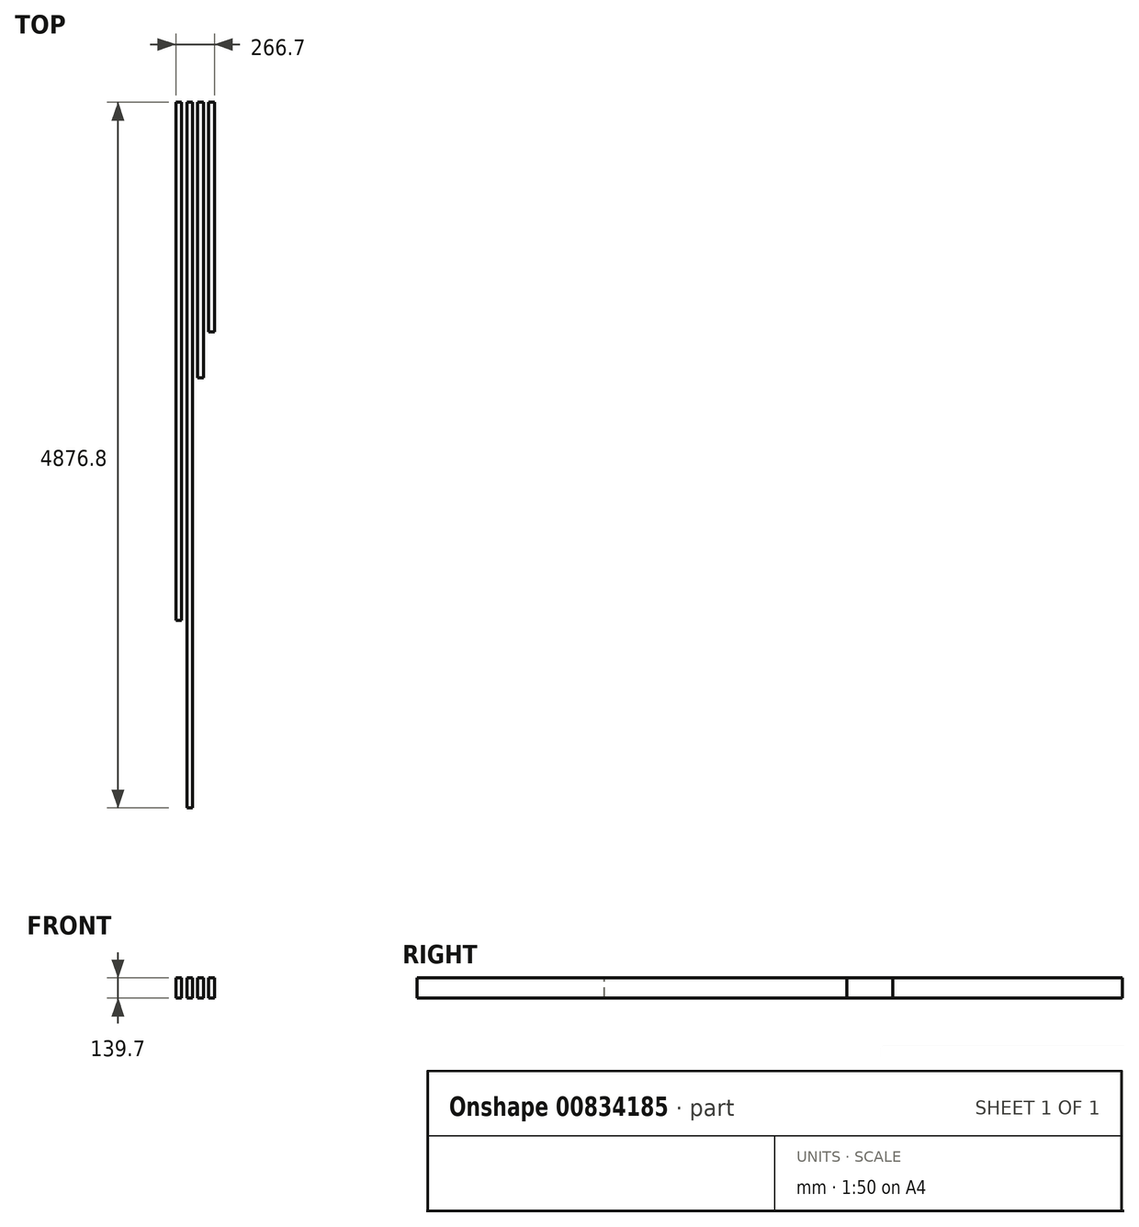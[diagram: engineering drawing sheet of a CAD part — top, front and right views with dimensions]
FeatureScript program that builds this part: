
annotation { "Feature Type Name" : "Feature", "Feature Type Description" : "" }
export const myFeature = defineFeature(function(context is Context, id is Id, definition is map)
    precondition{}
    {
        {
            var Q0;
            Q0=qCreatedBy(makeId("Front.planeOp"),FACE);
            var sketch = newSketch(context, id + "F0", { "sketchPlane" : qUnion([Q0])});
            skLineSegment(sketch, "E0.bottom", {"start": v(19.05, -69.85) * mm, "end": v(-19.05, -69.85) * mm});
            skLineSegment(sketch, "E0.top", {"start": v(19.05, 69.85) * mm, "end": v(-19.05, 69.85) * mm});
            skLineSegment(sketch, "E0.left", {"start": v(19.05, -69.85) * mm, "end": v(19.05, 69.85) * mm});
            skLineSegment(sketch, "E0.right", {"start": v(-19.05, -69.85) * mm, "end": v(-19.05, 69.85) * mm});
            skPoint(sketch, "E0.middle", {"position": v(0, 0) * mm});
            skLineSegment(sketch, "E1.1.0.0", {"start": v(57.15, -69.85) * mm, "end": v(57.15, 69.85) * mm});
            skLineSegment(sketch, "E1.1.0.1", {"start": v(95.25, 69.85) * mm, "end": v(57.15, 69.85) * mm});
            skLineSegment(sketch, "E1.1.0.2", {"start": v(95.25, -69.85) * mm, "end": v(95.25, 69.85) * mm});
            skLineSegment(sketch, "E1.1.0.3", {"start": v(95.25, -69.85) * mm, "end": v(57.15, -69.85) * mm});
            skLineSegment(sketch, "E1.2.0.0", {"start": v(133.35, -69.85) * mm, "end": v(133.35, 69.85) * mm});
            skLineSegment(sketch, "E1.2.0.1", {"start": v(171.45, 69.85) * mm, "end": v(133.35, 69.85) * mm});
            skLineSegment(sketch, "E1.2.0.2", {"start": v(171.45, -69.85) * mm, "end": v(171.45, 69.85) * mm});
            skLineSegment(sketch, "E1.2.0.3", {"start": v(171.45, -69.85) * mm, "end": v(133.35, -69.85) * mm});
            skLineSegment(sketch, "E1.direction1", {"start": v(-19.05, -69.85) * mm, "end": v(57.15, -69.85) * mm, "construction": true});
            skLineSegment(sketch, "E2.0.3.0", {"start": v(209.55, -69.85) * mm, "end": v(209.55, 69.85) * mm});
            skLineSegment(sketch, "E2.3.3.0", {"start": v(247.65, 69.85) * mm, "end": v(209.55, 69.85) * mm});
            skLineSegment(sketch, "E2.6.3.0", {"start": v(247.65, -69.85) * mm, "end": v(247.65, 69.85) * mm});
            skLineSegment(sketch, "E2.9.3.0", {"start": v(247.65, -69.85) * mm, "end": v(209.55, -69.85) * mm});
            skLineSegment(sketch, "E2.0.4.0", {"start": v(285.75, -69.85) * mm, "end": v(285.75, 69.85) * mm});
            skLineSegment(sketch, "E2.3.4.0", {"start": v(323.85, 69.85) * mm, "end": v(285.75, 69.85) * mm});
            skLineSegment(sketch, "E2.6.4.0", {"start": v(323.85, -69.85) * mm, "end": v(323.85, 69.85) * mm});
            skLineSegment(sketch, "E2.9.4.0", {"start": v(323.85, -69.85) * mm, "end": v(285.75, -69.85) * mm});
            skSolve(sketch);
        }
        {
            var Q0;
            Q0=makeQuery(id+"F0.imprint","IMPRINT",FACE,{"disambiguationData":[TD([[makeQuery(id+"F0.imprint","IMPRINT",EDGE,{"derivedFrom":sQuery(id+"F0.wireOp",EDGE,"E0.bottom")}),-1.0]])]});
            extrude(context, id + "F1", {"entities" : qUnion([Q0]), "depth" : 3581.4 * mm, "offsetDistance" : 25.4 * mm});
        }
        {
            var Q0;
            Q0=makeQuery(id+"F0.imprint","IMPRINT",FACE,{"disambiguationData":[TD([[makeQuery(id+"F0.imprint","IMPRINT",EDGE,{"derivedFrom":sQuery(id+"F0.wireOp",EDGE,"E1.1.0.0")}),-1.0]])]});
            extrude(context, id + "F2", {"entities" : qUnion([Q0]), "depth" : 4876.8 * mm, "offsetDistance" : 25.4 * mm});
        }
        {
            var Q0;
            Q0=makeQuery(id+"F0.imprint","IMPRINT",FACE,{"disambiguationData":[TD([[makeQuery(id+"F0.imprint","IMPRINT",EDGE,{"derivedFrom":sQuery(id+"F0.wireOp",EDGE,"E1.2.0.0")}),-1.0]])]});
            extrude(context, id + "F3", {"entities" : qUnion([Q0]), "depth" : 1905 * mm, "offsetDistance" : 25.4 * mm});
        }
        {
            var Q0;
            Q0=makeQuery(id+"F0.imprint","IMPRINT",FACE,{"disambiguationData":[TD([[makeQuery(id+"F0.imprint","IMPRINT",EDGE,{"derivedFrom":sQuery(id+"F0.wireOp",EDGE,"E2.0.3.0")}),-1.0]])]});
            extrude(context, id + "F4", {"entities" : qUnion([Q0]), "depth" : 1587.5 * mm, "offsetDistance" : 25.4 * mm});
        }
    });
